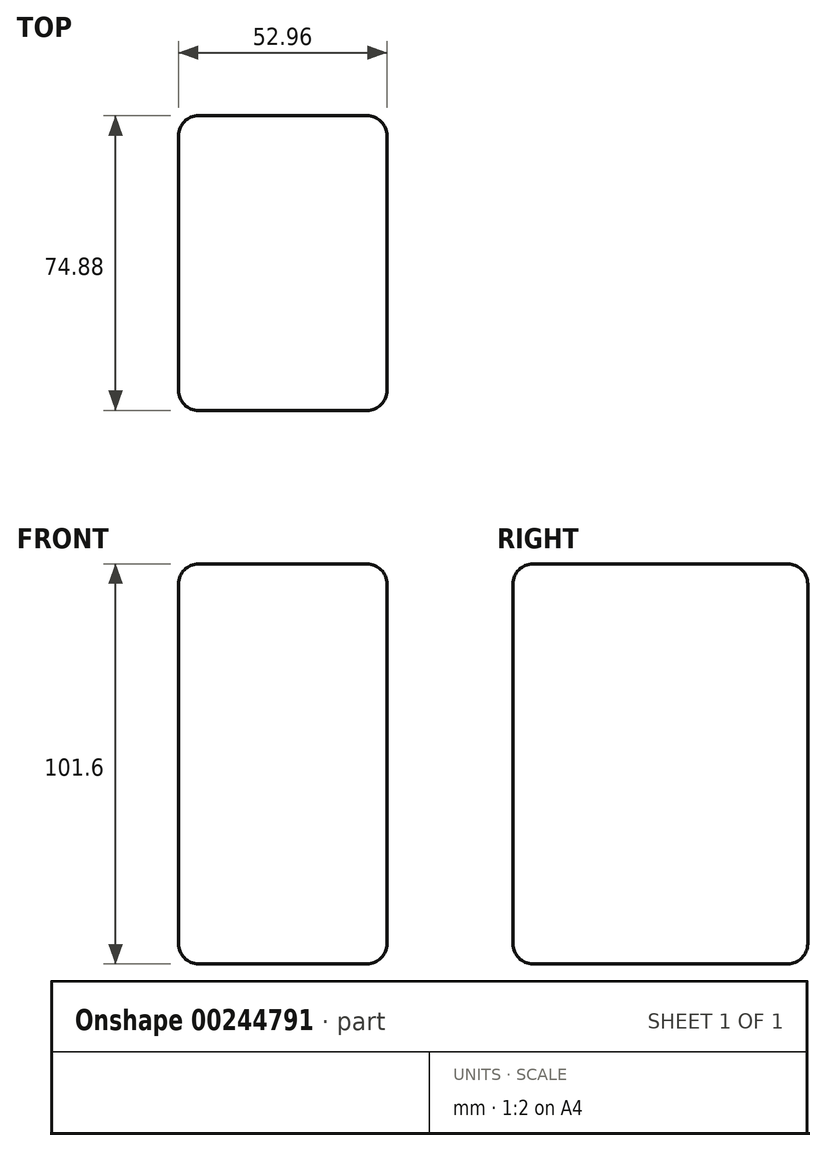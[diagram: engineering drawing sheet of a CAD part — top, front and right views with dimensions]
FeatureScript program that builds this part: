
annotation { "Feature Type Name" : "Feature", "Feature Type Description" : "" }
export const myFeature = defineFeature(function(context is Context, id is Id, definition is map)
    precondition{}
    {
        {
            var Q0;
            Q0=qCreatedBy(makeId("Top.planeOp"),FACE);
            var sketch = newSketch(context, id + "F0", { "sketchPlane" : qUnion([Q0])});
            skLineSegment(sketch, "E0.bottom", {"start": v(-29.04, 45.84) * mm, "end": v(23.92, 45.84) * mm});
            skLineSegment(sketch, "E0.top", {"start": v(-29.04, -29.04) * mm, "end": v(23.92, -29.04) * mm});
            skLineSegment(sketch, "E0.left", {"start": v(-29.04, 45.84) * mm, "end": v(-29.04, -29.04) * mm});
            skLineSegment(sketch, "E0.right", {"start": v(23.92, 45.84) * mm, "end": v(23.92, -29.04) * mm});
            skSolve(sketch);
        }
        {
            var Q0;
            Q0=makeQuery(id+"F0.imprint","IMPRINT",FACE,{"disambiguationData":[TD([[makeQuery(id+"F0.imprint","IMPRINT",EDGE,{"derivedFrom":sQuery(id+"F0.wireOp",EDGE,"E0.bottom")}),-1.0]])]});
            extrude(context, id + "F1", {"entities" : qUnion([Q0]), "depth" : 101.6 * mm});
        }
        {
            var Q0;
            Q0=makeQuery(id+"F1.opExtrude","SWEPT_EDGE",EDGE,{"disambiguationData":[OSD([sQuery(id+"F0.wireOp",EDGE,"E0.top"),sQuery(id+"F0.wireOp",EDGE,"E0.right")])]});
            var Q1;
            Q1=makeQuery(id+"F1.opExtrude","SWEPT_EDGE",EDGE,{"disambiguationData":[OSD([sQuery(id+"F0.wireOp",EDGE,"E0.bottom"),sQuery(id+"F0.wireOp",EDGE,"E0.right")])]});
            var Q2;
            Q2=makeQuery(id+"F1.opExtrude","SWEPT_EDGE",EDGE,{"disambiguationData":[OSD([sQuery(id+"F0.wireOp",EDGE,"E0.top"),sQuery(id+"F0.wireOp",EDGE,"E0.left")])]});
            var Q3;
            Q3=makeQuery(id+"F1.opExtrude","SWEPT_EDGE",EDGE,{"disambiguationData":[OSD([sQuery(id+"F0.wireOp",EDGE,"E0.bottom"),sQuery(id+"F0.wireOp",EDGE,"E0.left")])]});
            var Q4;
            Q4=makeQuery(id+"F1.opExtrude","CAP_EDGE",EDGE,{"disambiguationData":[OSD([sQuery(id+"F0.wireOp",EDGE,"E0.right")])],"isStart":false});
            var Q5;
            Q5=makeQuery(id+"F1.opExtrude","CAP_EDGE",EDGE,{"disambiguationData":[OSD([sQuery(id+"F0.wireOp",EDGE,"E0.bottom")])],"isStart":false});
            var Q6;
            Q6=makeQuery(id+"F1.opExtrude","CAP_EDGE",EDGE,{"disambiguationData":[OSD([sQuery(id+"F0.wireOp",EDGE,"E0.left")])],"isStart":false});
            var Q7;
            Q7=makeQuery(id+"F1.opExtrude","CAP_EDGE",EDGE,{"disambiguationData":[OSD([sQuery(id+"F0.wireOp",EDGE,"E0.top")])],"isStart":false});
            var Q8;
            Q8=makeQuery(id+"F1.opExtrude","CAP_EDGE",EDGE,{"disambiguationData":[OSD([sQuery(id+"F0.wireOp",EDGE,"E0.top")])],"isStart":true});
            var Q9;
            Q9=makeQuery(id+"F1.opExtrude","CAP_EDGE",EDGE,{"disambiguationData":[OSD([sQuery(id+"F0.wireOp",EDGE,"E0.right")])],"isStart":true});
            var Q10;
            Q10=makeQuery(id+"F1.opExtrude","CAP_EDGE",EDGE,{"disambiguationData":[OSD([sQuery(id+"F0.wireOp",EDGE,"E0.bottom")])],"isStart":true});
            var Q11;
            Q11=makeQuery(id+"F1.opExtrude","CAP_EDGE",EDGE,{"disambiguationData":[OSD([sQuery(id+"F0.wireOp",EDGE,"E0.left")])],"isStart":true});
            fillet(context, id + "F2", {"entities" : qUnion([Q0, Q1, Q2, Q3, Q4, Q5, Q6, Q7, Q8, Q9, Q10, Q11]), "radius" : 5.08 * mm, "tangentPropagation" : true, "allowEdgeOverflow" : false});
        }
    });
